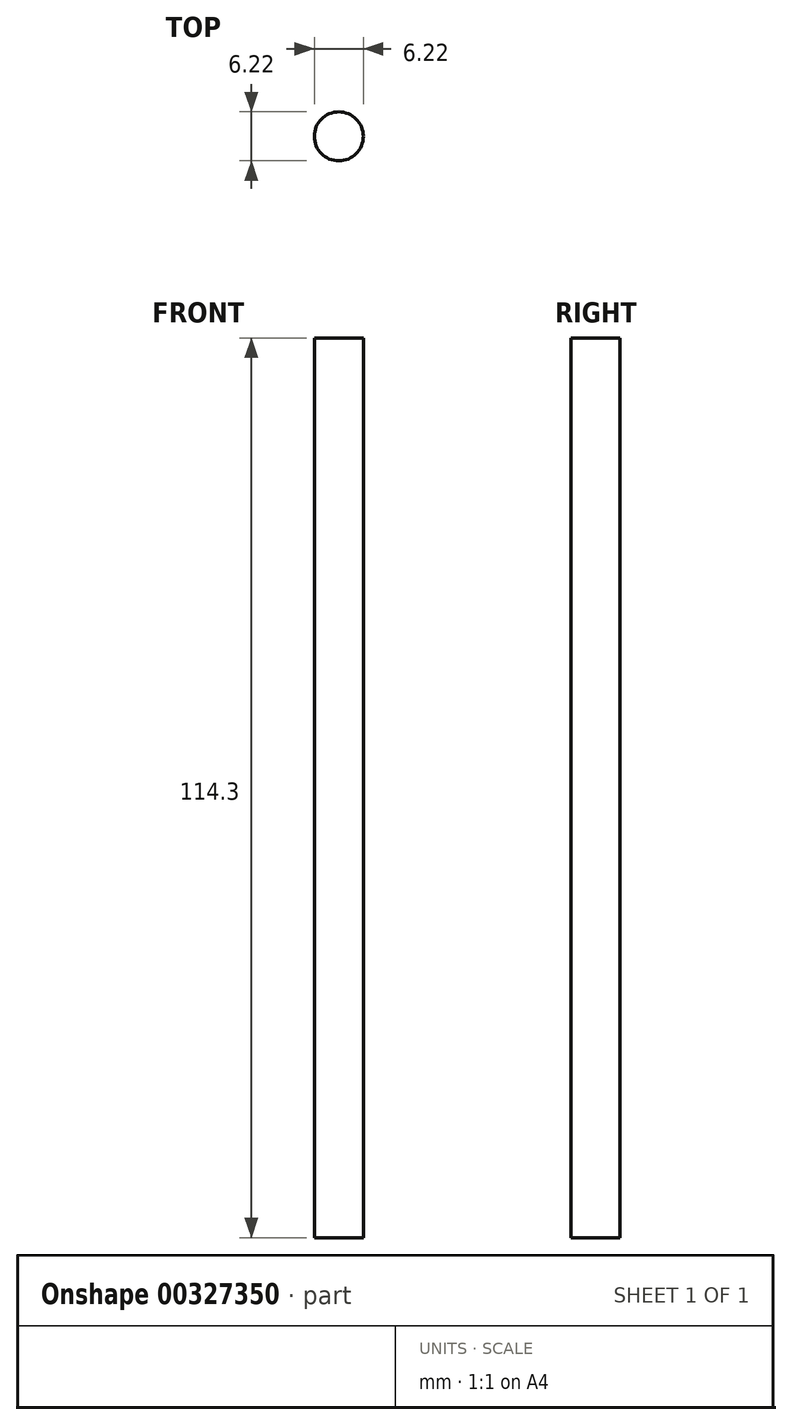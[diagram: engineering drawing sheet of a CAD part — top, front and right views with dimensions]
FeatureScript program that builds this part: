
annotation { "Feature Type Name" : "Feature", "Feature Type Description" : "" }
export const myFeature = defineFeature(function(context is Context, id is Id, definition is map)
    precondition{}
    {
        {
            var Q0;
            Q0=qCreatedBy(makeId("Top.planeOp"),FACE);
            var sketch = newSketch(context, id + "F0", { "sketchPlane" : qUnion([Q0])});
            skCircle(sketch, "E0", {"center": v(0, 0) * mm, "radius": 3.11 * mm});
            skSolve(sketch);
        }
        {
            var Q0;
            Q0=makeQuery(id+"F0.imprint","IMPRINT",FACE,{"disambiguationData":[TD([[makeQuery(id+"F0.imprint","IMPRINT",EDGE,{"derivedFrom":sQuery(id+"F0.wireOp",EDGE,"E0")}),1.0]])]});
            extrude(context, id + "F1", {"entities" : qUnion([Q0]), "depth" : 114.3 * mm});
        }
    });
